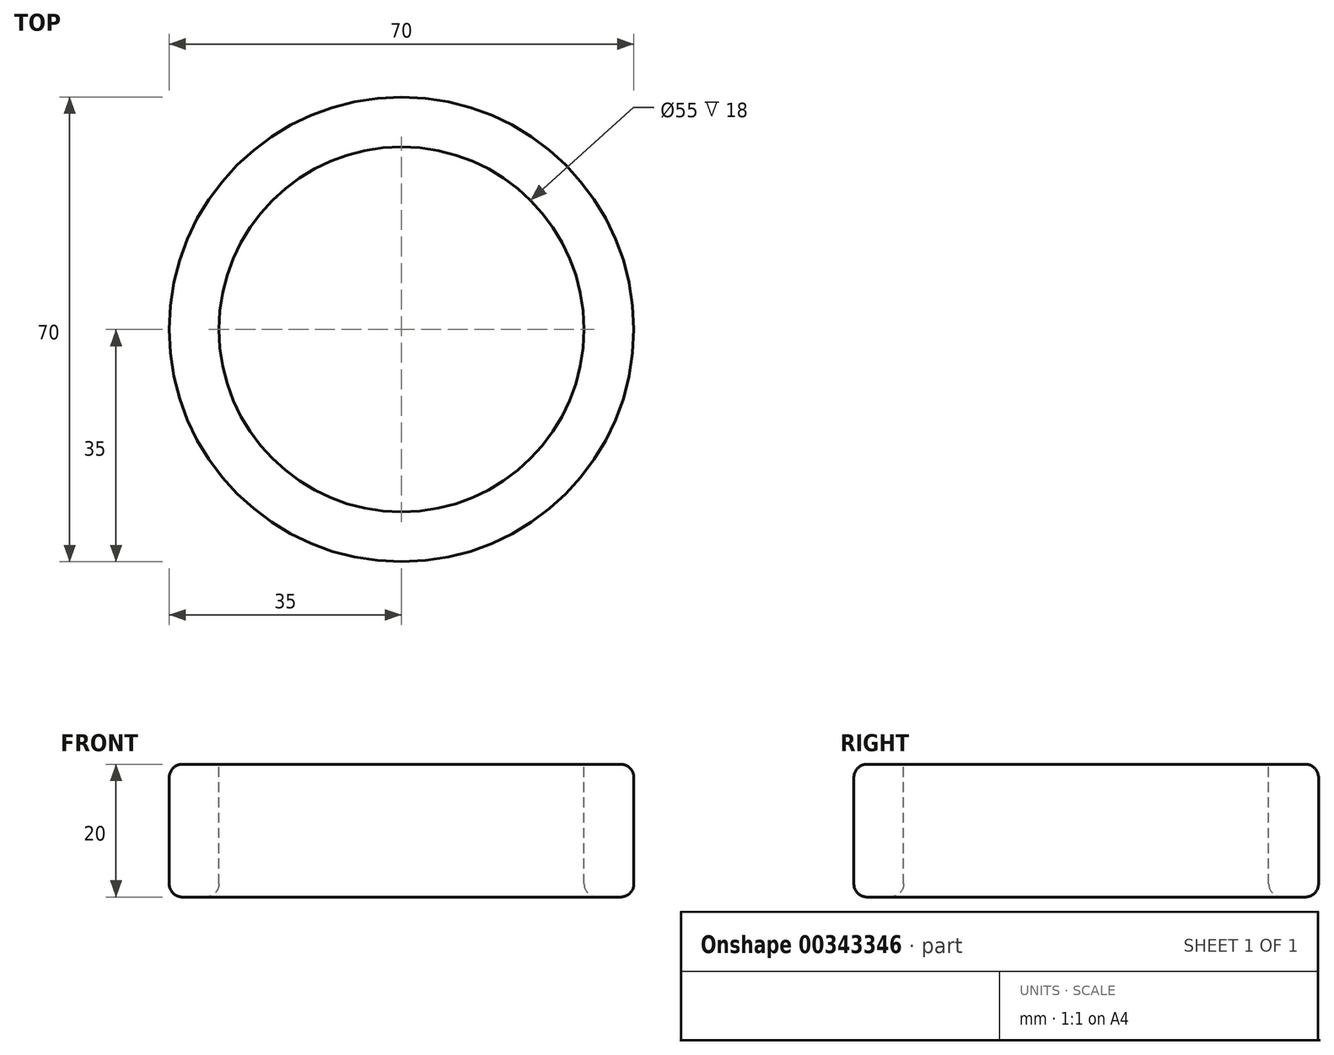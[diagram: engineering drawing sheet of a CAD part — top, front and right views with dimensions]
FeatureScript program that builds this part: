
annotation { "Feature Type Name" : "Feature", "Feature Type Description" : "" }
export const myFeature = defineFeature(function(context is Context, id is Id, definition is map)
    precondition{}
    {
        {
            var Q0;
            Q0=qCreatedBy(makeId("Top.planeOp"),FACE);
            var sketch = newSketch(context, id + "F0", { "sketchPlane" : qUnion([Q0])});
            skCircle(sketch, "E0", {"center": v(0, 0) * mm, "radius": 35 * mm});
            skSolve(sketch);
        }
        {
            var Q0;
            Q0=makeQuery(id+"F0.imprint","IMPRINT",FACE,{"disambiguationData":[TD([[makeQuery(id+"F0.imprint","IMPRINT",EDGE,{"derivedFrom":sQuery(id+"F0.wireOp",EDGE,"E0")}),1.0]])]});
            extrude(context, id + "F1", {"entities" : qUnion([Q0]), "depth" : 20 * mm});
        }
        {
            var Q0;
            Q0=makeQuery(id+"F1.opExtrude","CAP_FACE",FACE,{"disambiguationData":[OSD([sQuery(id+"F0.wireOp",EDGE,"E0")])],"isStart":false});
            var sketch = newSketch(context, id + "F2", { "sketchPlane" : qUnion([Q0])});
            skCircle(sketch, "E1", {"center": v(0, 0) * mm, "radius": 27.5 * mm});
            skSolve(sketch);
        }
        {
            var Q0;
            Q0=makeQuery(id+"F2.imprint","IMPRINT",FACE,{"disambiguationData":[TD([[makeQuery(id+"F2.imprint","IMPRINT",EDGE,{"derivedFrom":sQuery(id+"F2.wireOp",EDGE,"E1")}),1.0]])]});
            extrude(context, id + "F3", {"entities" : qUnion([Q0]), "operationType" : NewBodyOperationType.REMOVE, "oppositeDirection" : true, "depth" : 25 * mm});
        }
        {
            var Q0;
            Q0=makeQuery(id+"F3.boolean.opBoolean","COPY",EDGE,{"derivedFrom":makeQuery(id+"F3.opExtrude","CAP_EDGE",EDGE,{"disambiguationData":[OSD([sQuery(id+"F2.wireOp",EDGE,"E1")])],"isStart":true})});
            var Q1;
            Q1=makeQuery(id+"F3.boolean.opBoolean","INTERSECT",EDGE,{"derivedFrom":[makeQuery(id+"F1.opExtrude","CAP_FACE",FACE,{"disambiguationData":[OSD([sQuery(id+"F0.wireOp",EDGE,"E0")])],"isStart":true}),makeQuery(id+"F3.opExtrude","SWEPT_FACE",FACE,{"disambiguationData":[OSD([sQuery(id+"F2.wireOp",EDGE,"E1")])]})]});
            fillet(context, id + "F4", {"entities" : qUnion([Q0, Q1]), "radius" : 2 * mm, "tangentPropagation" : true, "allowEdgeOverflow" : false});
        }
        {
            var Q0;
            Q0=makeQuery(id+"F1.opExtrude","CAP_EDGE",EDGE,{"disambiguationData":[OSD([sQuery(id+"F0.wireOp",EDGE,"E0")])],"isStart":false});
            var Q1;
            Q1=makeQuery(id+"F1.opExtrude","CAP_EDGE",EDGE,{"disambiguationData":[OSD([sQuery(id+"F0.wireOp",EDGE,"E0")])],"isStart":true});
            fillet(context, id + "F5", {"entities" : qUnion([Q0, Q1]), "radius" : 2 * mm, "tangentPropagation" : true, "allowEdgeOverflow" : false});
        }
    });
